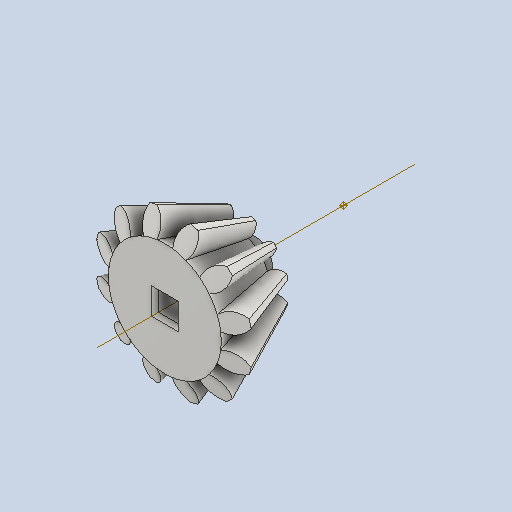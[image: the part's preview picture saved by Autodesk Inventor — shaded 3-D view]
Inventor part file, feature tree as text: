
AUTODESK INVENTOR PART (.ipt)
format: ipt  version: 2022 (Build 260153000, 153)  size: 1,043,456 bytes
history: native  units: in
note: dims shown in document units (in); Inventor stores cm internally (conversion verified against a paired STEP export)
features: other x30, sketch x3, extrude x2, chamfer x2, projected_geometry x1
ambient origin geometry x8: Origin, YZ Plane, XZ Plane, XY Plane, X Axis, Y Axis, Z Axis, Center Point
bodies: Solid1 (feature_tree)
feature tree (38):
  other  "Bevel Gear1"
  extrude  "Extrusion1"  TaperAngle=0.0deg  [1 undecoded]
  extrude  "Extrusion2"  TaperAngle=90.0deg  [1 undecoded]
  chamfer  "Chamfer2"  [1 undecoded]
  chamfer  "Chamfer4"  [1 undecoded]
  other  "Solid1::Bevel Gear1"
  other  "TaggingFeature1"
  other  "Teeth Body Sketch"
  other  "Start Sketch"
  other  "End Sketch"
  other  "End Sketch Right"
  other  "End Sketch Left"
  other  "Body Sketch"
  sketch  "Sketch6"  dims[d0=0.3937in d48=0.0in]
  other  "3D Sketch Right"
  other  "3D Sketch Left"
  other  "Mesh Plane"
  other  "Top Plane"
  other  "Mesh Plane2"
  other  "Tooth Plane"
  other  "End Plane"
  other  "End Plane Right"
  other  "End Plane Left"
  other  "Z Axis_1"
  other  "Top Point"
  other  "Start Point"
  other  "End Point"
  other  "Srf1"
  sketch  "Sketch8"  dims[d49=0.0in d50=90.0deg]
  sketch  "Sketch9"  dims[d52=0.0in d53=0.0in d54=0.0in d1=0.1329in d2=0.0in d3=0.0in d4=0.25in d5=0.125in d6=0.0in d10=0.0472in d11=0.125in d12=45.0deg d16=0.0236in d17=0.125in d18=45.0deg]
  projected_geometry  "Projected Loop1"
  other  "Srf1::Derived"
  other  "Start plane iMate"
  other  "Mesh iMate2"
  other  "Axis Angle iMate"
  other  "Axis iMate"
  other  "Mesh iMate"
  other  "Intersection iMate"
note: 4 required parameter values undecoded (feature->parameter linkage not recoverable at this tier; creation-order binding heuristic only, values carry confidence <= 0.55)
